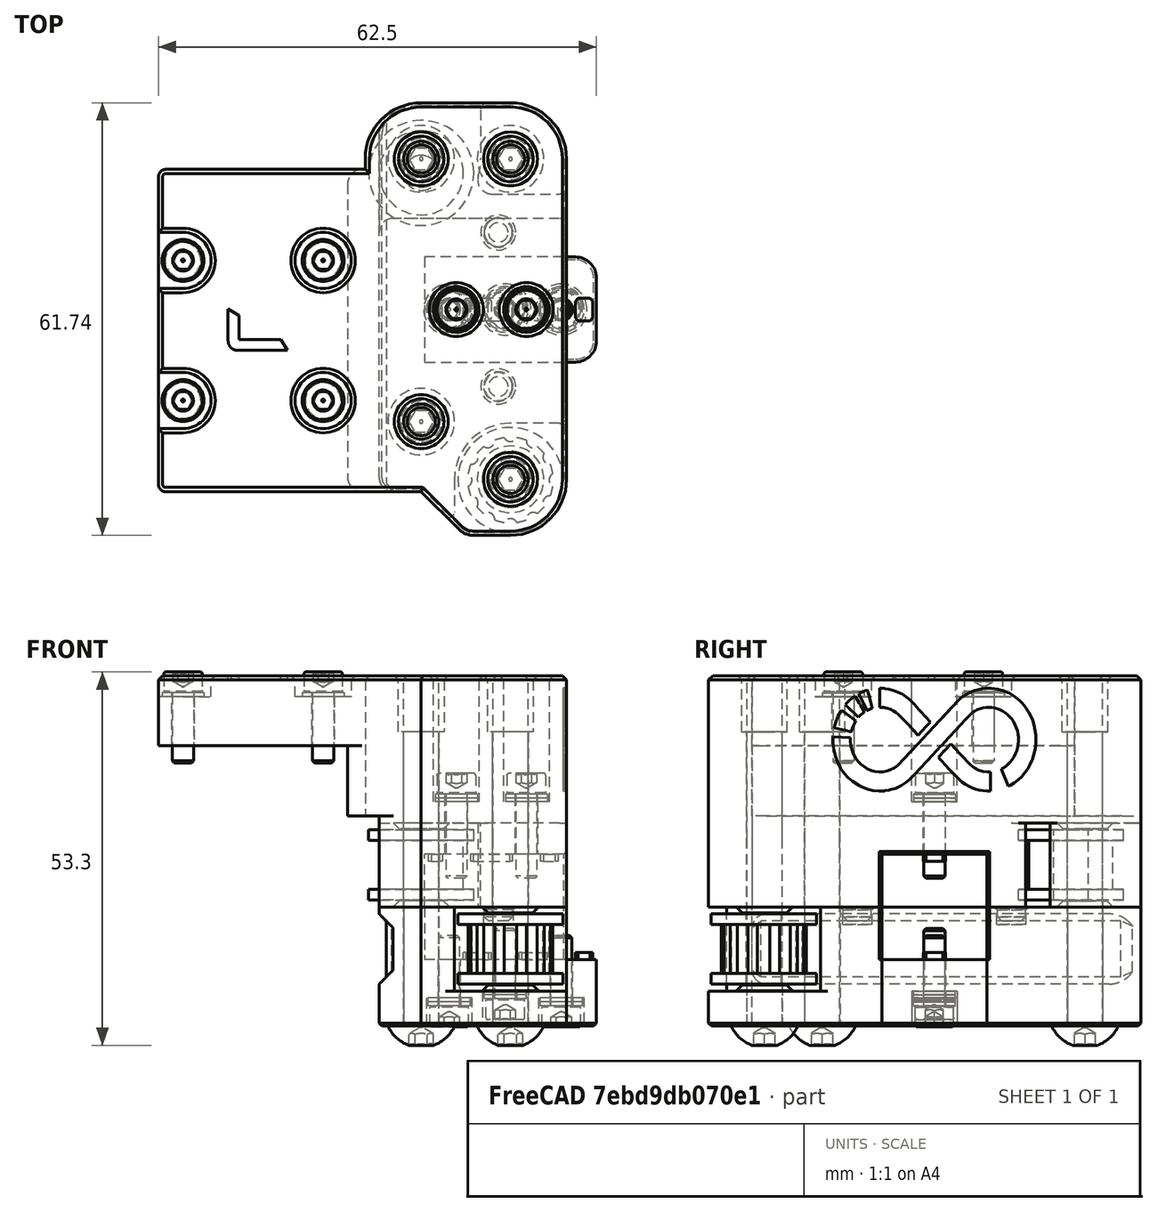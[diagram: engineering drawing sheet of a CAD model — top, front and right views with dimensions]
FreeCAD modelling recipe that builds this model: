
FCSTD DOCUMENT  (FreeCAD 0.19R24291 (Git))
Label: y-carrier-left-1515-assembly
License: Other
LicenseURL: GPL3
objects: Part::FeaturePython×27, Part::Feature×4, App::Part×1
note: 31 computed .brp shape members not serialized (recipe doc carries the construction recipe); baked Part::Feature solids carry a one-line shape summary decoded from their .brp

FEATURE [Part::Feature] Cut001002  label="smooth-idler"
  Placement = pos=(-2,0.5,0) rot=(0,0,1;0rad)
  shape: bbox 15 x 15 x 10 mm, 8 faces (baked)
FEATURE [Part::Feature] Cut002001001  label="20t-idler"
  Placement = pos=(0,-4.61,0) rot=(0,0,1;0rad)
  shape: bbox 15 x 15 x 10 mm, 31 faces (baked)
FEATURE [Part::FeaturePython] Screw003  label="M5x50-Screw"  # Fasteners workbench fastener (typed FeaturePython)
  Placement = pos=(9,-16,3) rot=(-1,0,0;3.14159rad)
  diameter = 3
  invert = true
  length = 11
  lengthCustom = 50
  matchOuter = true
  offset = 0
  thread = false
  type = 39
FEATURE [Part::FeaturePython] Screw004  label="M5x50-Screw004"  # Fasteners workbench fastener (typed FeaturePython)
  Placement = pos=(9,21.5,3) rot=(-1,0,0;3.14159rad)
  diameter = 3
  invert = true
  length = 11
  lengthCustom = 50
  matchOuter = true
  offset = 0
  thread = false
  type = 39
FEATURE [Part::FeaturePython] Screw005  label="M5x50-Screw005"  # Fasteners workbench fastener (typed FeaturePython)
  Placement = pos=(21.74,21.5,3) rot=(-1,0,0;3.14159rad)
  diameter = 3
  invert = true
  length = 11
  lengthCustom = 50
  matchOuter = true
  offset = 0
  thread = false
  type = 39
FEATURE [Part::FeaturePython] Screw006  label="M5x50-Screw003"  # Fasteners workbench fastener (typed FeaturePython)
  Placement = pos=(21.74,-24.24,3) rot=(-1,0,0;3.14159rad)
  diameter = 3
  invert = true
  length = 11
  lengthCustom = 50
  matchOuter = true
  offset = 0
  thread = false
  type = 39
FEATURE [Part::FeaturePython] Washer003  label="M3-Washer"  # Fasteners workbench fastener (typed FeaturePython)
  Placement = pos=(-25,-13,50) rot=(0,0,1;0rad)
  diameter = 4
  invert = false
  matchOuter = true
  offset = 0
  type = 5
FEATURE [Part::FeaturePython] Washer004  label="M3-Washer004"  # Fasteners workbench fastener (typed FeaturePython)
  Placement = pos=(-25,7,50) rot=(0,0,1;0rad)
  diameter = 4
  invert = false
  matchOuter = true
  offset = 0
  type = 5
FEATURE [Part::FeaturePython] Washer005  label="M3-Washer005"  # Fasteners workbench fastener (typed FeaturePython)
  Placement = pos=(-5,7,50) rot=(0,0,1;0rad)
  diameter = 4
  invert = false
  matchOuter = true
  offset = 0
  type = 5
FEATURE [Part::FeaturePython] Washer006  label="M3-Washer006"  # Fasteners workbench fastener (typed FeaturePython)
  Placement = pos=(-5,-13,50) rot=(0,0,1;0rad)
  diameter = 4
  invert = false
  matchOuter = true
  offset = 0
  type = 5
FEATURE [Part::FeaturePython] Screw007  label="M3x10-Screw"  # Fasteners workbench fastener (typed FeaturePython)
  Placement = pos=(-25,7,50.55) rot=(0,0,1;0rad)
  baseObject = -> Washer004 [Edge1]
  diameter = 4
  invert = false
  length = 3
  lengthCustom = 10
  matchOuter = true
  offset = 0
  thread = false
  type = 33
FEATURE [Part::FeaturePython] Screw008  label="M3x10-Screw005"  # Fasteners workbench fastener (typed FeaturePython)
  Placement = pos=(-25,-13,50.55) rot=(0,0,1;0rad)
  baseObject = -> Washer003 [Edge1]
  diameter = 4
  invert = false
  length = 3
  lengthCustom = 10
  matchOuter = true
  offset = 0
  thread = false
  type = 33
FEATURE [Part::FeaturePython] Screw009  label="M3x10-Screw004"  # Fasteners workbench fastener (typed FeaturePython)
  Placement = pos=(-5,-13,50.55) rot=(0,0,1;0rad)
  baseObject = -> Washer006 [Edge1]
  diameter = 4
  invert = false
  length = 3
  lengthCustom = 10
  matchOuter = true
  offset = 0
  thread = false
  type = 33
FEATURE [Part::FeaturePython] Screw010  label="M3x10-Screw006"  # Fasteners workbench fastener (typed FeaturePython)
  Placement = pos=(-5,7,50.55) rot=(0,0,1;0rad)
  baseObject = -> Washer005 [Edge1]
  diameter = 4
  invert = false
  length = 3
  lengthCustom = 10
  matchOuter = true
  offset = 0
  thread = false
  type = 33
FEATURE [Part::Feature] Chamfer030007001
  Placement = pos=(0,0,3) rot=(0,0,1;0rad)
  shape: bbox 31 x 61.74 x 17.85 mm, 119 faces (baked)
FEATURE [Part::Feature] Cut002001
  Placement = pos=(0,0,3) rot=(0,0,1;0rad)
  shape: bbox 58.24 x 61.74 x 35 mm, 468 faces (baked)
FEATURE [Part::FeaturePython] Washer  label="M3-Washer007"  # Fasteners workbench fastener (typed FeaturePython)
  Placement = pos=(13,0,7) rot=(-1,0,0;3.14159rad)
  baseObject = -> Chamfer030007001 [Edge6]
  diameter = 4
  invert = false
  matchOuter = true
  offset = 0
  type = 5
FEATURE [Part::FeaturePython] Washer007  label="M3-Washer009"  # Fasteners workbench fastener (typed FeaturePython)
  Placement = pos=(21,0,8) rot=(-1,0,0;3.14159rad)
  baseObject = -> Chamfer030007001 [Edge219]
  diameter = 4
  invert = false
  matchOuter = true
  offset = 0
  type = 5
FEATURE [Part::FeaturePython] Washer008  label="M3-Washer008"  # Fasteners workbench fastener (typed FeaturePython)
  Placement = pos=(29,0,7) rot=(-1,0,0;3.14159rad)
  baseObject = -> Chamfer030007001 [Edge217]
  diameter = 4
  invert = false
  matchOuter = true
  offset = 0
  type = 5
FEATURE [Part::FeaturePython] Washer009  label="M3-Washer010"  # Fasteners workbench fastener (typed FeaturePython)
  Placement = pos=(13,1e-16,6.45) rot=(-1,0,0;3.14159rad)
  baseObject = -> Washer [Edge1]
  diameter = 4
  invert = false
  matchOuter = true
  offset = 0
  type = 5
FEATURE [Part::FeaturePython] Washer010  label="M3-Washer011"  # Fasteners workbench fastener (typed FeaturePython)
  Placement = pos=(21,1e-16,7.45) rot=(-1,0,0;3.14159rad)
  baseObject = -> Washer007 [Edge1]
  diameter = 4
  invert = false
  matchOuter = true
  offset = 0
  type = 5
FEATURE [Part::FeaturePython] Washer011  label="M3-Washer012"  # Fasteners workbench fastener (typed FeaturePython)
  Placement = pos=(29,1e-16,6.45) rot=(-1,0,0;3.14159rad)
  baseObject = -> Washer008 [Edge1]
  diameter = 4
  invert = false
  matchOuter = true
  offset = 0
  type = 5
FEATURE [Part::FeaturePython] Screw  label="M3x10-Screw007"  # Fasteners workbench fastener (typed FeaturePython)
  Placement = pos=(13,1e-16,5.9) rot=(-1,0,0;3.14159rad)
  baseObject = -> Washer009 [Edge1]
  diameter = 4
  invert = false
  length = 3
  lengthCustom = 10
  matchOuter = true
  offset = 0
  thread = false
  type = 33
FEATURE [Part::FeaturePython] Screw011  label="M3x10-Screw008"  # Fasteners workbench fastener (typed FeaturePython)
  Placement = pos=(21,1e-16,6.9) rot=(-1,0,0;3.14159rad)
  baseObject = -> Washer010 [Edge1]
  diameter = 4
  invert = false
  length = 3
  lengthCustom = 10
  matchOuter = true
  offset = 0
  thread = false
  type = 33
FEATURE [Part::FeaturePython] Screw012  label="M3x10-Screw009"  # Fasteners workbench fastener (typed FeaturePython)
  Placement = pos=(29,1e-16,5.9) rot=(-1,0,0;3.14159rad)
  baseObject = -> Washer011 [Edge1]
  diameter = 4
  invert = false
  length = 3
  lengthCustom = 10
  matchOuter = true
  offset = 0
  thread = false
  type = 33
FEATURE [Part::FeaturePython] Washer012  label="M3-Washer013"  # Fasteners workbench fastener (typed FeaturePython)
  Placement = pos=(14,0,35) rot=(0,0,1;0rad)
  baseObject = -> Cut002001 [Edge1110]
  diameter = 4
  invert = false
  matchOuter = true
  offset = 0
  type = 5
FEATURE [Part::FeaturePython] Washer013  label="M3-Washer014"  # Fasteners workbench fastener (typed FeaturePython)
  Placement = pos=(24,0,35) rot=(0,0,1;0rad)
  baseObject = -> Cut002001 [Edge1112]
  diameter = 4
  invert = false
  matchOuter = true
  offset = 0
  type = 5
FEATURE [Part::FeaturePython] Washer014  label="M3-Washer015"  # Fasteners workbench fastener (typed FeaturePython)
  Placement = pos=(14,0,35.55) rot=(0,0,1;0rad)
  baseObject = -> Washer012 [Edge1]
  diameter = 4
  invert = false
  matchOuter = true
  offset = 0
  type = 5
FEATURE [Part::FeaturePython] Washer015  label="M3-Washer016"  # Fasteners workbench fastener (typed FeaturePython)
  Placement = pos=(24,0,35.55) rot=(0,0,1;0rad)
  baseObject = -> Washer013 [Edge1]
  diameter = 4
  invert = false
  matchOuter = true
  offset = 0
  type = 5
FEATURE [Part::FeaturePython] Screw013  label="M3x12-Screw"  # Fasteners workbench fastener (typed FeaturePython)
  Placement = pos=(14,0,36.1) rot=(0,0,1;0rad)
  baseObject = -> Washer014 [Edge1]
  diameter = 4
  invert = false
  length = 4
  lengthCustom = 12
  matchOuter = true
  offset = 0
  thread = false
  type = 33
FEATURE [Part::FeaturePython] Screw014  label="M3x12-Screw001"  # Fasteners workbench fastener (typed FeaturePython)
  Placement = pos=(24,0,36.1) rot=(0,0,1;0rad)
  baseObject = -> Washer015 [Edge1]
  diameter = 4
  invert = false
  length = 4
  lengthCustom = 12
  matchOuter = true
  offset = 0
  thread = false
  type = 33
FEATURE [App::Part] Part  label="Y-carrier-left"
  Group = -> [Cut001002,Cut002001001,Washer003,Washer004,Washer005,Screw007,Washer006,Screw009,Screw008,Screw010,Screw006,Screw004,Screw005,Screw003,Cut002001,Chamfer030007001,Washer011,Washer009,Washer007,Screw012,Screw011,Screw,Washer008,Washer010,Washer,Washer013,Washer014,Washer015,Screw014,Screw013,Washer012]
  Origin = -> Origin
